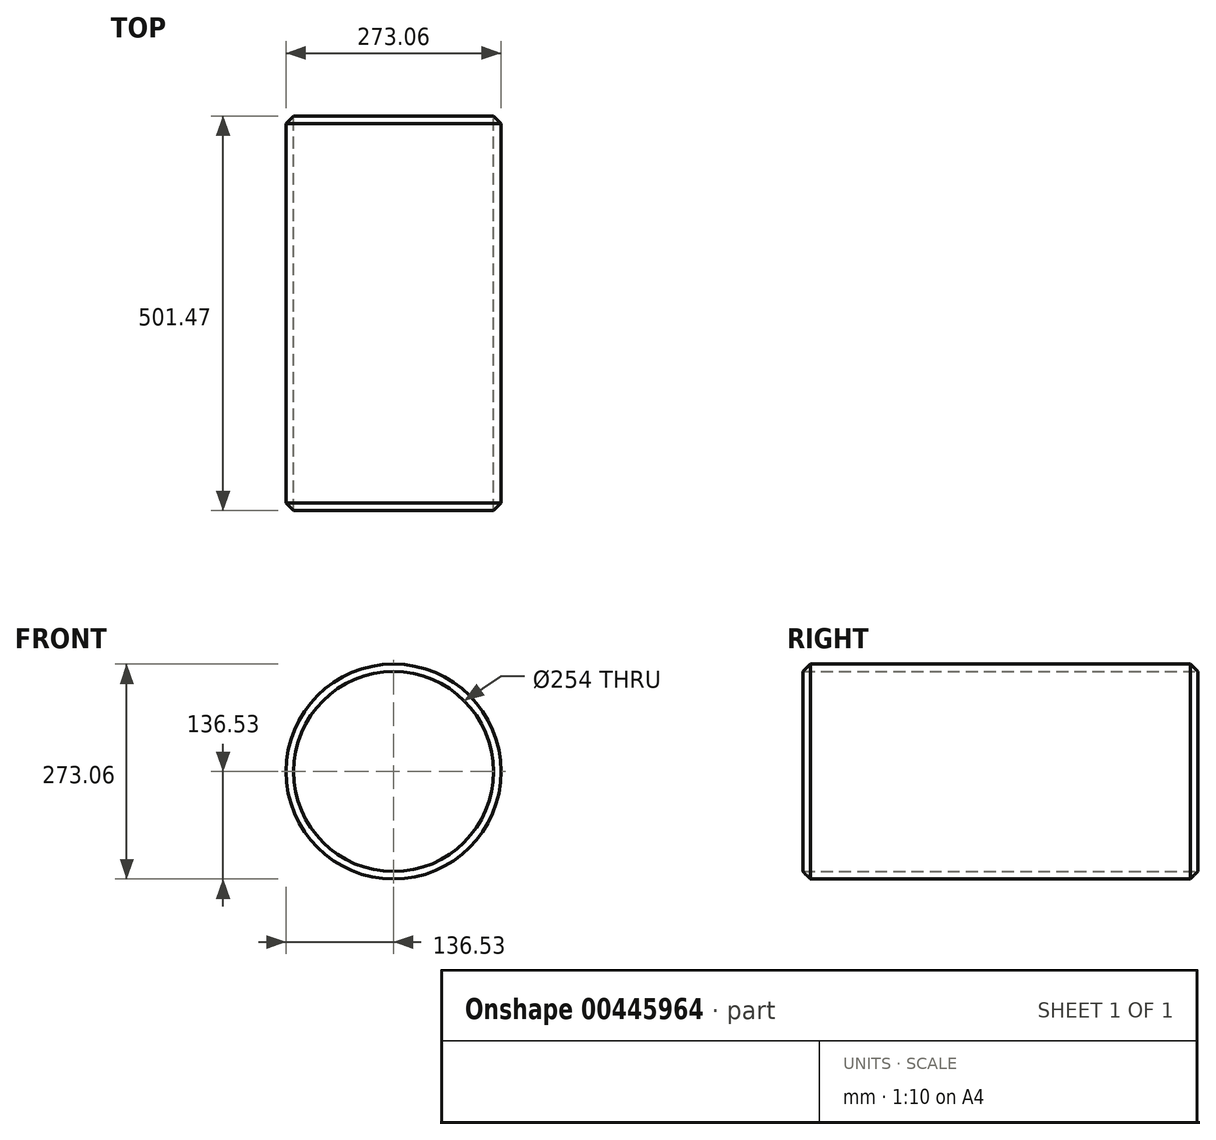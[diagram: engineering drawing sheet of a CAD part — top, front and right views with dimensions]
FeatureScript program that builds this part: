
annotation { "Feature Type Name" : "Feature", "Feature Type Description" : "" }
export const myFeature = defineFeature(function(context is Context, id is Id, definition is map)
    precondition{}
    {
        {
            var Q0;
            Q0=qCreatedBy(makeId("Front.planeOp"),FACE);
            var sketch = newSketch(context, id + "F0", { "sketchPlane" : qUnion([Q0])});
            skCircle(sketch, "E0", {"center": v(0, 0) * mm, "radius": 127 * mm});
            skCircle(sketch, "E1", {"center": v(0, 0) * mm, "radius": 136.53 * mm});
            skSolve(sketch);
        }
        {
            var Q0;
            Q0 = qSketchRegion(id + "F0", true);
            extrude(context, id + "F1", {"entities" : qUnion([Q0]), "depth" : 501.47 * mm, "offsetDistance" : 25.4 * mm});
        }
        {
            var Q0;
            Q0=makeQuery(id+"F1.opExtrude","CAP_EDGE",EDGE,{"disambiguationData":[OSD([sQuery(id+"F0.wireOp",EDGE,"E1")])],"isStart":false});
            chamfer(context, id + "F2", {"entities" : qUnion([Q0]), "width" : 9.52 * mm, "tangentPropagation" : true});
        }
        {
            var Q0;
            Q0=makeQuery(id+"F1.opExtrude","CAP_EDGE",EDGE,{"disambiguationData":[OSD([sQuery(id+"F0.wireOp",EDGE,"E1")])],"isStart":true});
            chamfer(context, id + "F3", {"entities" : qUnion([Q0]), "width" : 9.52 * mm, "tangentPropagation" : true});
        }
    });
